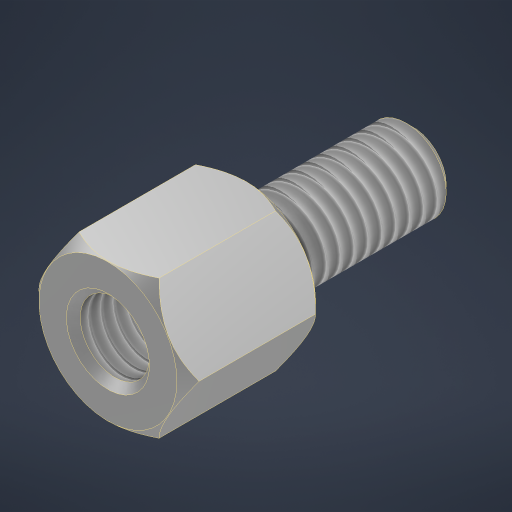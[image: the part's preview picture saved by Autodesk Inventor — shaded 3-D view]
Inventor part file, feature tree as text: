
AUTODESK INVENTOR PART (.ipt)
format: ipt  version: 2023 (Build 270158000, 158)  size: 279,040 bytes
history: native  units: in
note: dims shown in document units (in); Inventor stores cm internally (conversion verified against a paired STEP export)
features: thread x2, other x1
ambient origin geometry x8: Origin, YZ Plane, XZ Plane, XY Plane, X Axis, Y Axis, Z Axis, Center Point
bodies: Solid1 (feature_tree)
feature tree (3):
  thread  "Thread1"  [1 undecoded]
  thread  "Thread2"  [1 undecoded]
  other  "InnerChamfer"
note: 2 required parameter values undecoded (feature->parameter linkage not recoverable at this tier; creation-order binding heuristic only, values carry confidence <= 0.55)
